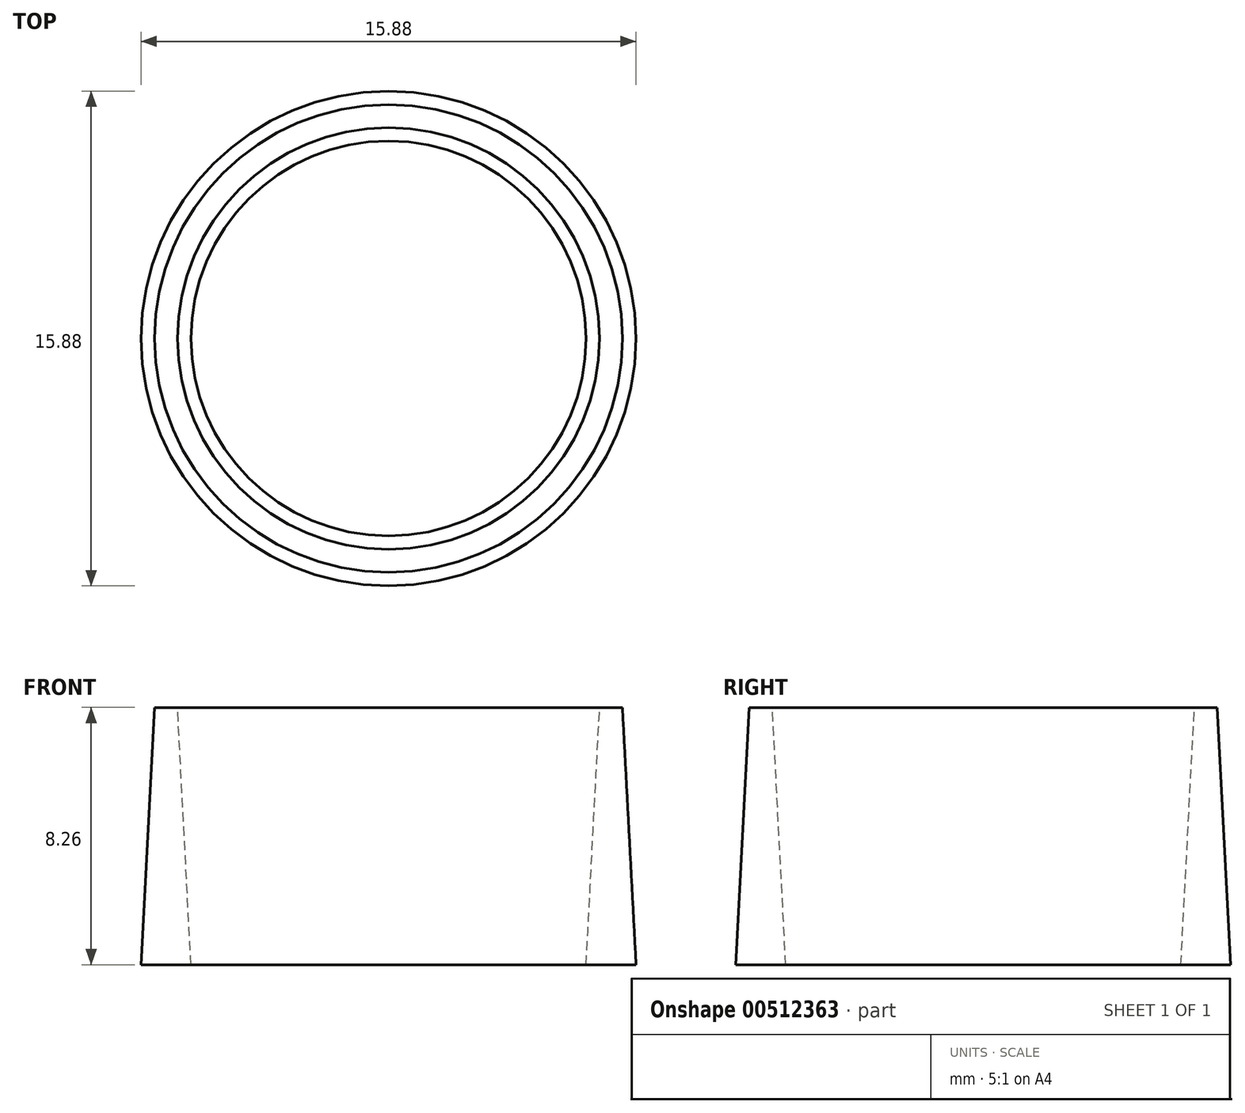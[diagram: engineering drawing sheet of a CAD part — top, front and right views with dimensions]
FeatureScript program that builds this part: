
annotation { "Feature Type Name" : "Feature", "Feature Type Description" : "" }
export const myFeature = defineFeature(function(context is Context, id is Id, definition is map)
    precondition{}
    {
        {
            var Q0;
            Q0=qCreatedBy(makeId("Top.planeOp"),FACE);
            var sketch = newSketch(context, id + "F0", { "sketchPlane" : qUnion([Q0])});
            skCircle(sketch, "E0", {"center": v(0, 0) * mm, "radius": 7.94 * mm});
            skCircle(sketch, "E1", {"center": v(0, 0) * mm, "radius": 6.34 * mm});
            skSolve(sketch);
        }
        {
            var Q0;
            Q0 = qSketchRegion(id + "F0", true);
            extrude(context, id + "F1", {"entities" : qUnion([Q0]), "depth" : 8.25 * mm, "hasDraft" : true, "draftAngle" : 3 * degree, "draftPullDirection" : true});
        }
    });
